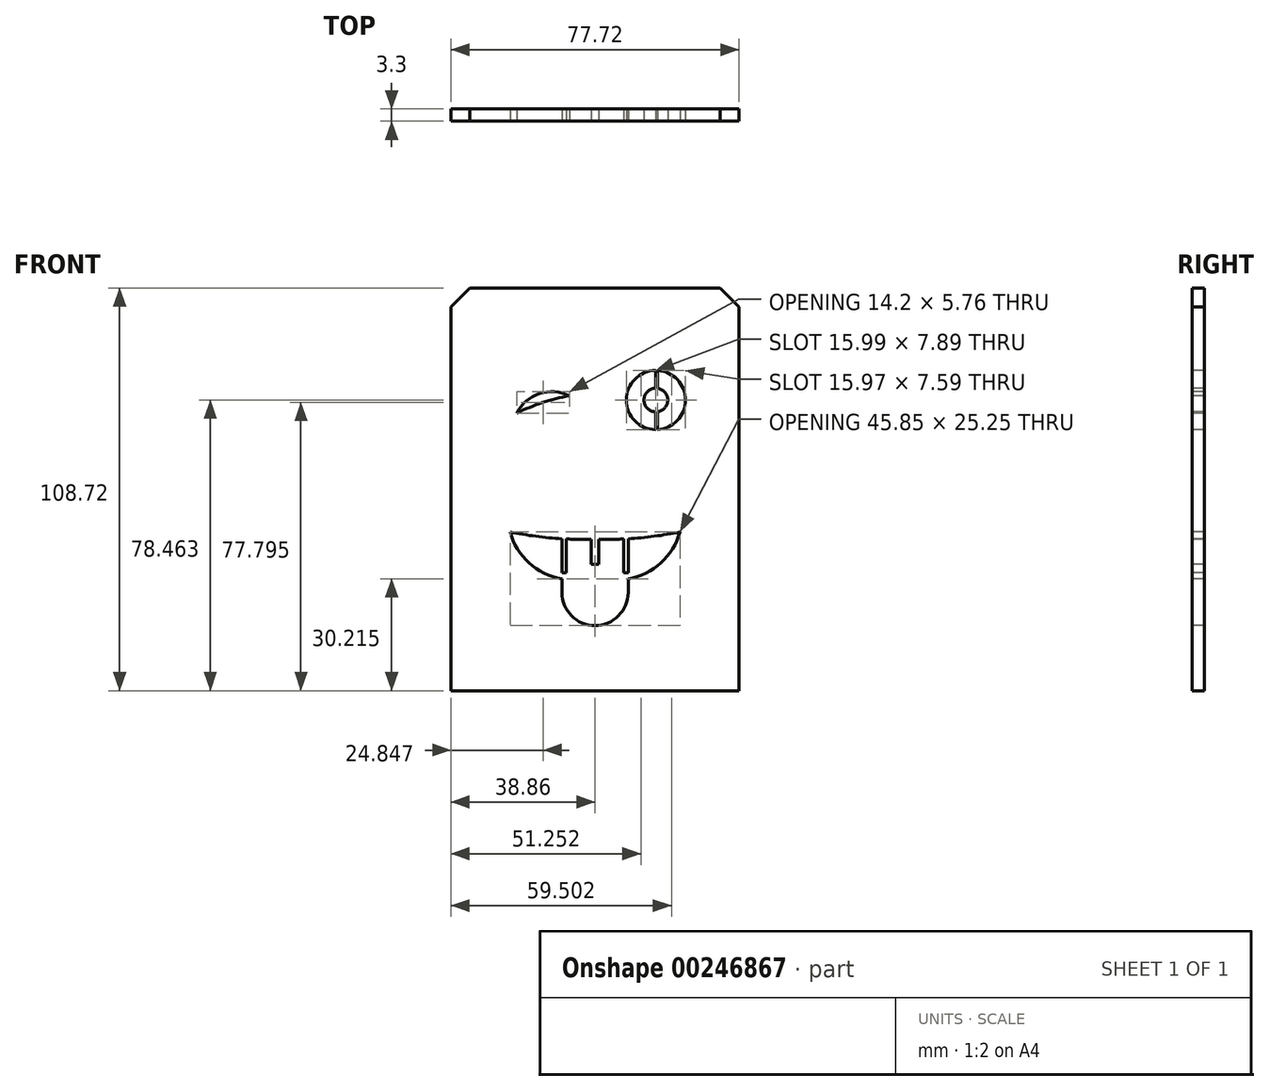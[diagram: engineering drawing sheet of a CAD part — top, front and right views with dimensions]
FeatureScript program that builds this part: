
annotation { "Feature Type Name" : "Feature", "Feature Type Description" : "" }
export const myFeature = defineFeature(function(context is Context, id is Id, definition is map)
    precondition{}
    {
        {
            var Q0;
            Q0=qCreatedBy(makeId("Front.planeOp"),FACE);
            var sketch = newSketch(context, id + "F0", { "sketchPlane" : qUnion([Q0])});
            skLineSegment(sketch, "E0.bottom", {"start": v(38.86, 54.36) * mm, "end": v(-38.86, 54.36) * mm});
            skLineSegment(sketch, "E0.top", {"start": v(38.86, -54.36) * mm, "end": v(-38.86, -54.36) * mm});
            skLineSegment(sketch, "E0.left", {"start": v(38.86, 54.36) * mm, "end": v(38.86, -54.36) * mm});
            skLineSegment(sketch, "E0.right", {"start": v(-38.86, 54.36) * mm, "end": v(-38.86, -54.36) * mm});
            skPoint(sketch, "E0.middle", {"position": v(0, 0) * mm});
            skSolve(sketch);
        }
        {
            var Q0;
            Q0=qSketchRegion(id+"F0",true);
            extrude(context, id + "F1", {"entities" : qUnion([Q0]), "depth" : 3.3 * mm});
        }
        {
            var Q0;
            Q0=makeQuery(id+"F1.opExtrude","CAP_FACE",FACE,{"disambiguationData":[OSD([sQuery(id+"F0.wireOp",EDGE,"E0.bottom"),sQuery(id+"F0.wireOp",EDGE,"E0.top"),sQuery(id+"F0.wireOp",EDGE,"E0.left"),sQuery(id+"F0.wireOp",EDGE,"E0.right")])],"isStart":false});
            var sketch = newSketch(context, id + "F2", { "sketchPlane" : qUnion([Q0])});
            skLineSegment(sketch, "E1", {"start": v(0, 57.24) * mm, "end": v(0, -57.24) * mm, "construction": true});
            skLineSegment(sketch, "E2", {"start": v(-50.8, 0) * mm, "end": v(50.8, 0) * mm, "construction": true});
            skArc(sketch, "E3", {"start": v(35.44, -3.57) * mm, "mid": v(31.46, -11.87) * mm, "end": v(32.26, -21.03) * mm});
            skLineSegment(sketch, "E4", {"start": v(15.88, -44.54) * mm, "end": v(0, -44.54) * mm, "construction": true});
            skArc(sketch, "E5", {"start": v(15.88, -44.54) * mm, "mid": v(30.2, -37.06) * mm, "end": v(32.26, -21.03) * mm});
            skArc(sketch, "E6", {"start": v(15.88, -44.54) * mm, "mid": v(7.78, -45.34) * mm, "end": v(0, -47.71) * mm});
            skArc(sketch, "E7.MirrorCS", {"start": v(-15.87, -44.54) * mm, "mid": v(-7.78, -45.34) * mm, "end": v(0, -47.71) * mm});
            skArc(sketch, "E8.MirrorCS", {"start": v(-15.87, -44.54) * mm, "mid": v(-30.2, -37.06) * mm, "end": v(-32.26, -21.03) * mm});
            skArc(sketch, "E9.MirrorCS", {"start": v(-35.44, -3.57) * mm, "mid": v(-31.46, -11.87) * mm, "end": v(-32.26, -21.03) * mm});
            skArc(sketch, "E10.MirrorCS", {"start": v(-35.44, 3.57) * mm, "mid": v(-31.46, 11.87) * mm, "end": v(-32.26, 21.03) * mm});
            skArc(sketch, "E11.MirrorCS", {"start": v(-15.88, 44.54) * mm, "mid": v(-30.2, 37.06) * mm, "end": v(-32.26, 21.03) * mm});
            skArc(sketch, "E12.MirrorCS", {"start": v(-15.88, 44.54) * mm, "mid": v(-7.78, 45.34) * mm, "end": v(0, 47.71) * mm});
            skArc(sketch, "E13.MirrorCS", {"start": v(15.87, 44.54) * mm, "mid": v(7.78, 45.34) * mm, "end": v(0, 47.71) * mm});
            skArc(sketch, "E14.MirrorCS", {"start": v(15.87, 44.54) * mm, "mid": v(30.2, 37.06) * mm, "end": v(32.26, 21.03) * mm});
            skArc(sketch, "E15.MirrorCS", {"start": v(35.44, 3.57) * mm, "mid": v(31.46, 11.87) * mm, "end": v(32.26, 21.03) * mm});
            skArc(sketch, "E16", {"start": v(35.44, 3.57) * mm, "mid": v(34.41, 0) * mm, "end": v(35.44, -3.57) * mm});
            skPoint(sketch, "E17.orphan", {"position": v(39.69, 0) * mm});
            skArc(sketch, "E18.MirrorCS", {"start": v(-35.44, 3.57) * mm, "mid": v(-34.41, 0) * mm, "end": v(-35.44, -3.57) * mm});
            skPoint(sketch, "E19.orphan", {"position": v(-39.69, 0) * mm});
            skSolve(sketch);
        }
        {
            var Q0;
            Q0=makeQuery(id+"F2.imprint","IMPRINT",FACE,{"disambiguationData":[TD([[makeQuery(id+"F2.imprint","IMPRINT",EDGE,{"derivedFrom":sQuery(id+"F2.wireOp",EDGE,"E3")}),1.0]])]});
            var sketch = newSketch(context, id + "F3", { "sketchPlane" : qUnion([Q0])});
            skFitSpline(sketch, "E20", {"points": [v(-34.74, -25) * mm, v(-17.68, -23.14) * mm, v(0, -25.84) * mm, v(18.3, -28) * mm, v(33.6, -24.4) * mm], "startDerivative": vector(68.08, 28.42) * mm, "endDerivative": vector(41.75, 55.86) * mm});
            skArc(sketch, "E21.0", {"start": v(15.88, -44.54) * mm, "mid": v(28.97, -38.63) * mm, "end": v(33.2, -24.9) * mm});
            skArc(sketch, "E22.0", {"start": v(-15.87, -44.54) * mm, "mid": v(-29.14, -38.43) * mm, "end": v(-33.13, -24.38) * mm});
            skArc(sketch, "E23.0", {"start": v(15.88, -44.54) * mm, "mid": v(7.78, -45.34) * mm, "end": v(0, -47.71) * mm});
            skArc(sketch, "E23.1", {"start": v(-15.87, -44.54) * mm, "mid": v(-7.78, -45.34) * mm, "end": v(0, -47.71) * mm});
            skPoint(sketch, "E24.orphan", {"position": v(-32.26, -21.03) * mm});
            skLineSegment(sketch, "E25.bottom", {"start": v(23.58, -32.65) * mm, "end": v(5.44, -32.65) * mm, "construction": true});
            skLineSegment(sketch, "E25.top", {"start": v(23.58, -12.55) * mm, "end": v(5.44, -12.55) * mm, "construction": true});
            skLineSegment(sketch, "E25.left", {"start": v(23.58, -32.65) * mm, "end": v(23.58, -12.55) * mm, "construction": true});
            skLineSegment(sketch, "E25.right", {"start": v(5.44, -32.65) * mm, "end": v(5.44, -12.55) * mm, "construction": true});
            skArc(sketch, "E26", {"start": v(6.5, -26.77) * mm, "mid": v(6.6, -19.6) * mm, "end": v(5.44, -12.55) * mm});
            skArc(sketch, "E27", {"start": v(23.58, -12.55) * mm, "mid": v(22.47, -20.37) * mm, "end": v(22.78, -28.26) * mm});
            skLineSegment(sketch, "E28", {"start": v(0.57, -13.45) * mm, "end": v(5.44, -12.55) * mm});
            skLineSegment(sketch, "E29", {"start": v(28.46, 0) * mm, "end": v(0.57, 0) * mm, "construction": true});
            skArc(sketch, "E30", {"start": v(-2.4, -8.48) * mm, "mid": v(-2.65, -12) * mm, "end": v(0.57, -13.45) * mm});
            skArc(sketch, "E31", {"start": v(0, -10.42) * mm, "mid": v(-0.23, -8.24) * mm, "end": v(-2.4, -8.48) * mm});
            skArc(sketch, "E32", {"start": v(0, -10.42) * mm, "mid": v(-0.04, -11.92) * mm, "end": v(1.4, -12.35) * mm});
            skArc(sketch, "E33", {"start": v(1.4, -12.35) * mm, "mid": v(5.55, -5.86) * mm, "end": v(0.57, 0) * mm});
            skLineSegment(sketch, "E34", {"start": v(14.51, 0) * mm, "end": v(14.51, -12.55) * mm, "construction": true});
            skArc(sketch, "E35.MirrorCS", {"start": v(27.61, -12.35) * mm, "mid": v(23.47, -5.86) * mm, "end": v(28.46, 0) * mm});
            skLineSegment(sketch, "E36.MirrorCS", {"start": v(28.46, -13.45) * mm, "end": v(23.58, -12.55) * mm});
            skArc(sketch, "E37.MirrorCS", {"start": v(31.42, -8.48) * mm, "mid": v(31.67, -12) * mm, "end": v(28.46, -13.45) * mm});
            skArc(sketch, "E38.MirrorCS", {"start": v(29.02, -10.42) * mm, "mid": v(29.25, -8.24) * mm, "end": v(31.42, -8.48) * mm});
            skArc(sketch, "E39.MirrorCS", {"start": v(29.02, -10.42) * mm, "mid": v(29.06, -11.92) * mm, "end": v(27.61, -12.35) * mm});
            skArc(sketch, "E40", {"start": v(0.57, 0) * mm, "mid": v(5.65, -0.6) * mm, "end": v(10.76, -0.93) * mm});
            skLineSegment(sketch, "E41", {"start": v(10.76, -0.93) * mm, "end": v(8.47, 9.06) * mm});
            skLineSegment(sketch, "E42", {"start": v(8.47, 9.06) * mm, "end": v(6.8, 8.68) * mm});
            skArc(sketch, "E43", {"start": v(7.7, 9.94) * mm, "mid": v(5.6, 10.49) * mm, "end": v(6.8, 8.68) * mm});
            skLineSegment(sketch, "E44", {"start": v(14.51, 0) * mm, "end": v(14.77, 8.31) * mm, "construction": true});
            skLineSegment(sketch, "E45.MirrorCS", {"start": v(18.26, -0.93) * mm, "end": v(21.1, 8.66) * mm});
            skLineSegment(sketch, "E46.MirrorCS", {"start": v(21.1, 8.66) * mm, "end": v(22.75, 8.18) * mm});
            skArc(sketch, "E47.MirrorCS", {"start": v(21.93, 9.5) * mm, "mid": v(24.07, 9.9) * mm, "end": v(22.75, 8.18) * mm});
            skArc(sketch, "E48", {"start": v(7.7, 9.94) * mm, "mid": v(12.62, 15.22) * mm, "end": v(14.1, 22.28) * mm});
            skArc(sketch, "E49", {"start": v(15.59, 22.28) * mm, "mid": v(17.1, 15.06) * mm, "end": v(21.93, 9.5) * mm});
            skLineSegment(sketch, "E50", {"start": v(14.1, 22.28) * mm, "end": v(12.75, 29.94) * mm});
            skLineSegment(sketch, "E51", {"start": v(12.75, 29.94) * mm, "end": v(10.25, 29.5) * mm});
            skLineSegment(sketch, "E52", {"start": v(10.25, 29.5) * mm, "end": v(10.04, 30.72) * mm});
            skLineSegment(sketch, "E53", {"start": v(10.04, 30.72) * mm, "end": v(12.66, 31.3) * mm});
            skLineSegment(sketch, "E54", {"start": v(12.66, 31.3) * mm, "end": v(12.12, 34.79) * mm});
            skLineSegment(sketch, "E55", {"start": v(12.12, 34.79) * mm, "end": v(14.24, 35.11) * mm});
            skLineSegment(sketch, "E56", {"start": v(14.24, 35.11) * mm, "end": v(14.8, 31.45) * mm});
            skLineSegment(sketch, "E57", {"start": v(14.8, 31.45) * mm, "end": v(17.72, 31.9) * mm});
            skLineSegment(sketch, "E58", {"start": v(17.72, 31.9) * mm, "end": v(17.99, 30.17) * mm});
            skLineSegment(sketch, "E59", {"start": v(17.99, 30.17) * mm, "end": v(14.89, 29.68) * mm});
            skLineSegment(sketch, "E60", {"start": v(14.89, 29.68) * mm, "end": v(15.59, 22.28) * mm});
            skArc(sketch, "E61.trimOffspring", {"start": v(18.26, -0.93) * mm, "mid": v(23.37, -0.6) * mm, "end": v(28.46, 0) * mm});
            skPoint(sketch, "E62.orphan", {"position": v(18.2, -1.17) * mm});
            skLineSegment(sketch, "E63", {"start": v(8.48, -4.98) * mm, "end": v(9.12, -7.41) * mm});
            skLineSegment(sketch, "E64", {"start": v(9.77, -9.85) * mm, "end": v(10.94, -9.54) * mm});
            skLineSegment(sketch, "E65", {"start": v(12.72, -9.06) * mm, "end": v(12.26, -7.34) * mm});
            skLineSegment(sketch, "E66", {"start": v(11.56, -4.7) * mm, "end": v(10.33, -4.82) * mm});
            skLineSegment(sketch, "E67", {"start": v(9.75, -4.87) * mm, "end": v(10.34, -7.13) * mm});
            skLineSegment(sketch, "E68", {"start": v(10.34, -7.13) * mm, "end": v(9.12, -7.41) * mm});
            skLineSegment(sketch, "E69", {"start": v(10.33, -4.82) * mm, "end": v(10.9, -7.06) * mm});
            skLineSegment(sketch, "E70", {"start": v(10.9, -7.06) * mm, "end": v(12.14, -6.89) * mm});
            skLineSegment(sketch, "E71", {"start": v(9.29, -8.05) * mm, "end": v(10.46, -7.73) * mm});
            skLineSegment(sketch, "E72", {"start": v(10.46, -7.73) * mm, "end": v(10.94, -9.54) * mm});
            skLineSegment(sketch, "E73", {"start": v(11.57, -9.37) * mm, "end": v(11.12, -7.64) * mm});
            skLineSegment(sketch, "E74", {"start": v(11.12, -7.64) * mm, "end": v(12.26, -7.34) * mm});
            skLineSegment(sketch, "E75.trimOffspring", {"start": v(12.14, -6.89) * mm, "end": v(11.56, -4.7) * mm});
            skLineSegment(sketch, "E76.trimOffspring", {"start": v(9.75, -4.87) * mm, "end": v(8.48, -4.98) * mm});
            skLineSegment(sketch, "E77.trimOffspring", {"start": v(9.29, -8.05) * mm, "end": v(9.77, -9.85) * mm});
            skLineSegment(sketch, "E78.trimOffspring", {"start": v(11.57, -9.37) * mm, "end": v(12.72, -9.06) * mm});
            skLineSegment(sketch, "E79.MirrorCS", {"start": v(17.46, -4.7) * mm, "end": v(18.69, -4.82) * mm});
            skLineSegment(sketch, "E80.MirrorCS", {"start": v(19.27, -4.87) * mm, "end": v(18.68, -7.13) * mm});
            skLineSegment(sketch, "E81.MirrorCS", {"start": v(17.45, -9.37) * mm, "end": v(17.9, -7.64) * mm});
            skLineSegment(sketch, "E82.MirrorCS", {"start": v(18.68, -7.13) * mm, "end": v(19.9, -7.41) * mm});
            skLineSegment(sketch, "E83.MirrorCS", {"start": v(17.9, -7.64) * mm, "end": v(16.76, -7.34) * mm});
            skLineSegment(sketch, "E84.MirrorCS", {"start": v(18.69, -4.82) * mm, "end": v(18.12, -7.06) * mm});
            skLineSegment(sketch, "E85.MirrorCS", {"start": v(16.88, -6.89) * mm, "end": v(17.46, -4.7) * mm});
            skLineSegment(sketch, "E86.MirrorCS", {"start": v(18.12, -7.06) * mm, "end": v(16.88, -6.89) * mm});
            skLineSegment(sketch, "E87.MirrorCS", {"start": v(19.27, -4.87) * mm, "end": v(20.54, -4.98) * mm});
            skLineSegment(sketch, "E88.MirrorCS", {"start": v(20.54, -4.98) * mm, "end": v(19.9, -7.41) * mm});
            skLineSegment(sketch, "E89.MirrorCS", {"start": v(19.73, -8.05) * mm, "end": v(18.56, -7.73) * mm});
            skLineSegment(sketch, "E90.MirrorCS", {"start": v(19.73, -8.05) * mm, "end": v(19.25, -9.85) * mm});
            skLineSegment(sketch, "E91.MirrorCS", {"start": v(19.25, -9.85) * mm, "end": v(18.08, -9.54) * mm});
            skLineSegment(sketch, "E92.MirrorCS", {"start": v(18.56, -7.73) * mm, "end": v(18.08, -9.54) * mm});
            skLineSegment(sketch, "E93.MirrorCS", {"start": v(17.45, -9.37) * mm, "end": v(16.3, -9.06) * mm});
            skLineSegment(sketch, "E94.MirrorCS", {"start": v(16.3, -9.06) * mm, "end": v(16.76, -7.34) * mm});
            skArc(sketch, "E95", {"start": v(14.28, 11.97) * mm, "mid": v(12.23, 10.98) * mm, "end": v(11.15, 8.98) * mm});
            skLineSegment(sketch, "E96", {"start": v(14.28, 11.97) * mm, "end": v(14.28, 8.98) * mm});
            skLineSegment(sketch, "E97", {"start": v(15.17, 4.65) * mm, "end": v(15.17, 7.88) * mm});
            skLineSegment(sketch, "E98", {"start": v(18.4, 8.98) * mm, "end": v(15.17, 8.98) * mm});
            skLineSegment(sketch, "E99", {"start": v(11.1, 7.88) * mm, "end": v(14.28, 7.88) * mm});
            skLineSegment(sketch, "E100.trimOffspring", {"start": v(15.17, 8.98) * mm, "end": v(15.17, 11.98) * mm});
            skLineSegment(sketch, "E101.trimOffspring", {"start": v(15.17, 7.88) * mm, "end": v(18.43, 7.88) * mm});
            skLineSegment(sketch, "E102.trimOffspring", {"start": v(14.28, 7.88) * mm, "end": v(14.28, 4.66) * mm});
            skLineSegment(sketch, "E103.trimOffspring", {"start": v(14.28, 8.98) * mm, "end": v(11.15, 8.98) * mm});
            skArc(sketch, "E104.trimOffspring", {"start": v(11.1, 7.88) * mm, "mid": v(12.14, 5.73) * mm, "end": v(14.28, 4.66) * mm});
            skArc(sketch, "E105.trimOffspring", {"start": v(18.4, 8.98) * mm, "mid": v(17.28, 11.01) * mm, "end": v(15.17, 11.98) * mm});
            skArc(sketch, "E106.trimOffspring", {"start": v(15.17, 4.65) * mm, "mid": v(17.37, 5.7) * mm, "end": v(18.43, 7.88) * mm});
            skLineSegment(sketch, "E107.left", {"start": v(12.04, -27.4) * mm, "end": v(12.04, -21.48) * mm});
            skLineSegment(sketch, "E107.right", {"start": v(16, -27.8) * mm, "end": v(16, -21.48) * mm});
            skArc(sketch, "E108", {"start": v(16, -21.48) * mm, "mid": v(14.02, -19.5) * mm, "end": v(12.04, -21.48) * mm});
            skLineSegment(sketch, "E109", {"start": v(12.04, -27.4) * mm, "end": v(16, -27.8) * mm});
            skArc(sketch, "E110.0", {"start": v(-35.44, -3.57) * mm, "mid": v(-31.46, -11.87) * mm, "end": v(-32.26, -21.03) * mm, "construction": true});
            skArc(sketch, "E110.1", {"start": v(15.87, 44.54) * mm, "mid": v(7.78, 45.34) * mm, "end": v(0, 47.71) * mm});
            skArc(sketch, "E110.2", {"start": v(-15.88, 44.54) * mm, "mid": v(-30.2, 37.06) * mm, "end": v(-32.26, 21.03) * mm, "construction": true});
            skArc(sketch, "E110.3", {"start": v(-35.44, 3.57) * mm, "mid": v(-34.41, 0) * mm, "end": v(-35.44, -3.57) * mm, "construction": true});
            skArc(sketch, "E110.4", {"start": v(-35.44, 3.57) * mm, "mid": v(-31.46, 11.87) * mm, "end": v(-32.26, 21.03) * mm});
            skArc(sketch, "E110.5", {"start": v(-15.88, 44.54) * mm, "mid": v(-7.78, 45.34) * mm, "end": v(0, 47.71) * mm});
            skArc(sketch, "E111", {"start": v(-17.1, 9.66) * mm, "mid": v(-3.37, 14.89) * mm, "end": v(1.5, 28.74) * mm});
            skArc(sketch, "E112", {"start": v(-17.1, 9.66) * mm, "mid": v(-26.87, 8.42) * mm, "end": v(-35.44, 3.57) * mm});
            skArc(sketch, "E113", {"start": v(15.87, 44.54) * mm, "mid": v(5.2, 39.82) * mm, "end": v(1.5, 28.74) * mm});
            skArc(sketch, "E114.trimOffspring", {"start": v(-15.88, 44.54) * mm, "mid": v(-30.2, 37.06) * mm, "end": v(-32.26, 21.03) * mm});
            skArc(sketch, "E115", {"start": v(-24.92, -22.89) * mm, "mid": v(-23.55, -16.2) * mm, "end": v(-24.4, -9.44) * mm});
            skFitSpline(sketch, "E116", {"points": [v(-24.4, -9.44) * mm, v(-26.98, -10.38) * mm, v(-27.97, -8.39) * mm, v(-29.93, -8.52) * mm, v(-30.92, -6) * mm, v(-32.1, -5.52) * mm, v(-32.53, -4.18) * mm, v(-32.18, -3.27) * mm, v(-31.84, -4.44) * mm, v(-31.05, -4.83) * mm, v(-31.49, -2) * mm, v(-30.88, -2.14) * mm, v(-30.1, -5.05) * mm, v(-29.45, -3.57) * mm, v(-28.71, -3.66) * mm, v(-29.54, -5.78) * mm, v(-29.23, -7.17) * mm, v(-27.54, -7.04) * mm, v(-26.28, -8.52) * mm, v(-24.4, -7.6) * mm], "startDerivative": vector(-46.53, -30.94) * mm, "endDerivative": vector(36.03, 29.74) * mm});
            skArc(sketch, "E117", {"start": v(-24.4, -7.6) * mm, "mid": v(-24.93, -4.98) * mm, "end": v(-25.9, -2.49) * mm});
            skFitSpline(sketch, "E118", {"points": [v(-25.9, -2.49) * mm, v(-27.5, -1.49) * mm, v(-28.76, -1.49) * mm, v(-29.23, 0) * mm, v(-31.14, 0) * mm, v(-30.8, 3.42) * mm, v(-29.97, 3.55) * mm, v(-30.27, 1.77) * mm, v(-29.54, 1.72) * mm, v(-28.8, 4.59) * mm, v(-27.67, 4.37) * mm, v(-28.28, 1.98) * mm, v(-27.84, 0) * mm, v(-27.2, 2.46) * mm, v(-25.9, 2.37) * mm, v(-25.9, 0) * mm, v(-24.11, -2.49) * mm, v(-22.72, -5.26) * mm, v(-21.68, -4.18) * mm, v(-23.16, 1.33) * mm, v(-20.82, 1.46) * mm, v(-20.82, 3.02) * mm], "startDerivative": vector(-33.14, 31.82) * mm, "endDerivative": vector(-15.18, 49.9) * mm});
            skFitSpline(sketch, "E119", {"points": [v(-20.82, 3.02) * mm, v(-19.2, 3.92) * mm, v(-20.04, 5.84) * mm, v(-20.82, 8.3) * mm, v(-20.04, 8.38) * mm, v(-19.62, 6.46) * mm, v(-18.62, 5.34) * mm, v(-18.96, 7.3) * mm, v(-18.2, 7.55) * mm, v(-18.12, 4.13) * mm, v(-19.33, 2.25) * mm, v(-19.46, 0.87) * mm, v(-20.82, 0) * mm, v(-20.04, -3.35) * mm, v(-16.32, 0) * mm, v(-17.1, 1.46) * mm, v(-15.74, 3.02) * mm, v(-15.45, 5.84) * mm, v(-14.49, 5.55) * mm, v(-14.82, 3.02) * mm, v(-14.53, 1.46) * mm, v(-13.36, 4) * mm, v(-12.02, 3.02) * mm, v(-14.2, 0) * mm, v(-17.1, -4.06) * mm, v(-17.1, -7.4) * mm, v(-14.36, -5.44) * mm, v(-14.57, -4.1) * mm, v(-12.78, -3.22) * mm, v(-12.53, -1.68) * mm, v(-10.44, -0.8) * mm, v(-10.27, 1.46) * mm, v(-9.35, 0) * mm, v(-8.6, 3.02) * mm, v(-8.1, 0) * mm, v(-9.44, -1.26) * mm, v(-11.31, -3.26) * mm, v(-13.15, -4.6) * mm, v(-13.36, -6.6) * mm, v(-15.78, -8.94) * mm], "startDerivative": vector(94.65, 30.69) * mm, "endDerivative": vector(-102.82, -69.25) * mm});
            skArc(sketch, "E120", {"start": v(-15.78, -8.94) * mm, "mid": v(-16.8, -16.14) * mm, "end": v(-15.78, -23.34) * mm});
            skFitSpline(sketch, "E121", {"points": [v(-22.4, -11.55) * mm, v(-21.43, -13.07) * mm, v(-21.4, -14.11) * mm, v(-20.72, -14.36) * mm, v(-20.54, -13.59) * mm, v(-20.94, -12.02) * mm, v(-21.71, -11.06) * mm, v(-22.67, -10.07) * mm, v(-22.4, -11.55) * mm]});
            skFitSpline(sketch, "E122", {"points": [v(-18.38, -10.1) * mm, v(-19.09, -11.5) * mm, v(-19.21, -12.7) * mm, v(-19.15, -14.02) * mm, v(-18.84, -14.6) * mm, v(-18.38, -14.05) * mm, v(-18.26, -13.1) * mm, v(-18.56, -12.32) * mm, v(-18.29, -11.28) * mm, v(-17.6, -10.38) * mm, v(-18.38, -10.1) * mm]});
            skFitSpline(sketch, "E123", {"points": [v(-20.3, -15.78) * mm, v(-20.35, -17.1) * mm, v(-20.9, -18.47) * mm, v(-21.8, -19.67) * mm, v(-21.9, -21.46) * mm, v(-20.45, -21.43) * mm, v(-19.64, -20.38) * mm, v(-19.43, -18.84) * mm, v(-19.7, -17.85) * mm, v(-19.7, -16.37) * mm, v(-19.43, -15.38) * mm, v(-20.3, -15.78) * mm]});
            skCircle(sketch, "E124", {"center": v(-15.88, 27.08) * mm, "radius": 13.34 * mm});
            skSolve(sketch);
        }
        {
            var Q0;
            Q0=qSketchRegion(id+"F3",true);
            extrude(context, id + "F4", {"entities" : qUnion([Q0]), "operationType" : NewBodyOperationType.ADD, "oppositeDirection" : true, "depth" : 3.3 * mm});
        }
        {
            var Q0;
            Q0=makeQuery(id+"F1.opExtrude","SWEPT_EDGE",EDGE,{"disambiguationData":[OSD([sQuery(id+"F0.wireOp",EDGE,"E0.bottom"),sQuery(id+"F0.wireOp",EDGE,"E0.right")])]});
            var Q1;
            Q1=makeQuery(id+"F1.opExtrude","SWEPT_EDGE",EDGE,{"disambiguationData":[OSD([sQuery(id+"F0.wireOp",EDGE,"E0.bottom"),sQuery(id+"F0.wireOp",EDGE,"E0.left")])]});
            chamfer(context, id + "F5", {"entities" : qUnion([Q0, Q1]), "width" : 5.08 * mm, "tangentPropagation" : true});
        }
        {
            var Q0;
            Q0=makeQuery(id+"F2.imprint","IMPRINT",FACE,{"disambiguationData":[TD([[makeQuery(id+"F2.imprint","IMPRINT",EDGE,{"derivedFrom":sQuery(id+"F2.wireOp",EDGE,"E3")}),-1.0]])]});
            var sketch = newSketch(context, id + "F6", { "sketchPlane" : qUnion([Q0])});
            skArc(sketch, "E125", {"start": v(-6.91, 25.22) * mm, "mid": v(-14.98, 25.81) * mm, "end": v(-21.11, 20.55) * mm});
            skArc(sketch, "E126", {"start": v(-6.91, 25.22) * mm, "mid": v(-14.18, 23.4) * mm, "end": v(-21.11, 20.55) * mm});
            skArc(sketch, "E127", {"start": v(16.34, 32.1) * mm, "mid": v(8.44, 24.1) * mm, "end": v(16.34, 16.1) * mm});
            skArc(sketch, "E128", {"start": v(16.34, 27.3) * mm, "mid": v(13.24, 24.1) * mm, "end": v(16.34, 20.9) * mm});
            skLineSegment(sketch, "E129.left", {"start": v(16.34, 32.1) * mm, "end": v(16.34, 27.3) * mm});
            skLineSegment(sketch, "E129.right", {"start": v(16.85, 32.09) * mm, "end": v(16.85, 27.28) * mm});
            skLineSegment(sketch, "E130.left", {"start": v(16.34, 20.9) * mm, "end": v(16.34, 16.1) * mm});
            skLineSegment(sketch, "E130.right", {"start": v(16.85, 20.93) * mm, "end": v(16.85, 16.12) * mm});
            skArc(sketch, "E131.trimOffspring", {"start": v(16.85, 20.93) * mm, "mid": v(19.64, 24.1) * mm, "end": v(16.85, 27.28) * mm});
            skPoint(sketch, "E130.bottom.start.orphan", {"position": v(16.34, 21.48) * mm});
            skArc(sketch, "E132.trimOffspring", {"start": v(16.85, 16.12) * mm, "mid": v(24.44, 24.1) * mm, "end": v(16.85, 32.09) * mm});
            skPoint(sketch, "E133.orphan", {"position": v(16.85, 15.43) * mm});
            skArc(sketch, "E134", {"start": v(1.04, -13.51) * mm, "mid": v(4.41, -13.51) * mm, "end": v(7.79, -13.4) * mm});
            skArc(sketch, "E135", {"start": v(8.96, -24.2) * mm, "mid": v(17.78, -19.88) * mm, "end": v(22.92, -11.52) * mm});
            skArc(sketch, "E136", {"start": v(0, -36.77) * mm, "mid": v(6.33, -34.14) * mm, "end": v(8.96, -27.81) * mm});
            skLineSegment(sketch, "E137", {"start": v(0, -36.77) * mm, "end": v(-10.81, -36.77) * mm, "construction": true});
            skLineSegment(sketch, "E138", {"start": v(8.96, -27.81) * mm, "end": v(8.96, -24.2) * mm});
            skLineSegment(sketch, "E139.top", {"start": v(1.04, -20.2) * mm, "end": v(0, -20.2) * mm});
            skLineSegment(sketch, "E139.left", {"start": v(1.04, -13.51) * mm, "end": v(1.04, -20.2) * mm});
            skPoint(sketch, "E140.orphan", {"position": v(0, -13.49) * mm});
            skArc(sketch, "E141.MirrorCS", {"start": v(-8.96, -24.2) * mm, "mid": v(-17.78, -19.88) * mm, "end": v(-22.92, -11.52) * mm});
            skArc(sketch, "E142.MirrorCS", {"start": v(-1.04, -13.51) * mm, "mid": v(-4.41, -13.51) * mm, "end": v(-7.79, -13.4) * mm});
            skLineSegment(sketch, "E143.MirrorCS", {"start": v(-1.04, -13.51) * mm, "end": v(-1.04, -20.2) * mm});
            skArc(sketch, "E144.MirrorCS", {"start": v(0, -36.77) * mm, "mid": v(-6.33, -34.14) * mm, "end": v(-8.96, -27.81) * mm});
            skLineSegment(sketch, "E145.MirrorCS", {"start": v(-8.96, -27.81) * mm, "end": v(-8.96, -24.2) * mm});
            skLineSegment(sketch, "E146.MirrorCS", {"start": v(-1.04, -20.2) * mm, "end": v(0, -20.2) * mm});
            skLineSegment(sketch, "E147.top", {"start": v(8.96, -22.5) * mm, "end": v(7.79, -22.5) * mm});
            skLineSegment(sketch, "E147.left", {"start": v(8.96, -13.34) * mm, "end": v(8.96, -22.5) * mm});
            skLineSegment(sketch, "E147.right", {"start": v(7.79, -13.4) * mm, "end": v(7.79, -22.5) * mm});
            skArc(sketch, "E148.trimOffspring", {"start": v(8.96, -13.34) * mm, "mid": v(15.97, -12.67) * mm, "end": v(22.92, -11.52) * mm});
            skLineSegment(sketch, "E149.MirrorCS", {"start": v(-7.79, -13.4) * mm, "end": v(-7.79, -22.5) * mm});
            skLineSegment(sketch, "E150.MirrorCS", {"start": v(-8.96, -13.34) * mm, "end": v(-8.96, -22.5) * mm});
            skLineSegment(sketch, "E151.MirrorCS", {"start": v(-8.96, -22.5) * mm, "end": v(-7.79, -22.5) * mm});
            skArc(sketch, "E152.trimOffspring", {"start": v(-8.96, -13.34) * mm, "mid": v(-15.97, -12.67) * mm, "end": v(-22.92, -11.52) * mm});
            skSolve(sketch);
        }
        {
            var Q0;
            Q0=qSketchRegion(id+"F6",true);
            extrude(context, id + "F7", {"entities" : qUnion([Q0]), "operationType" : NewBodyOperationType.REMOVE, "endBound" : BoundingType.THROUGH_ALL, "oppositeDirection" : true, "depth" : 25.4 * mm});
        }
    });
